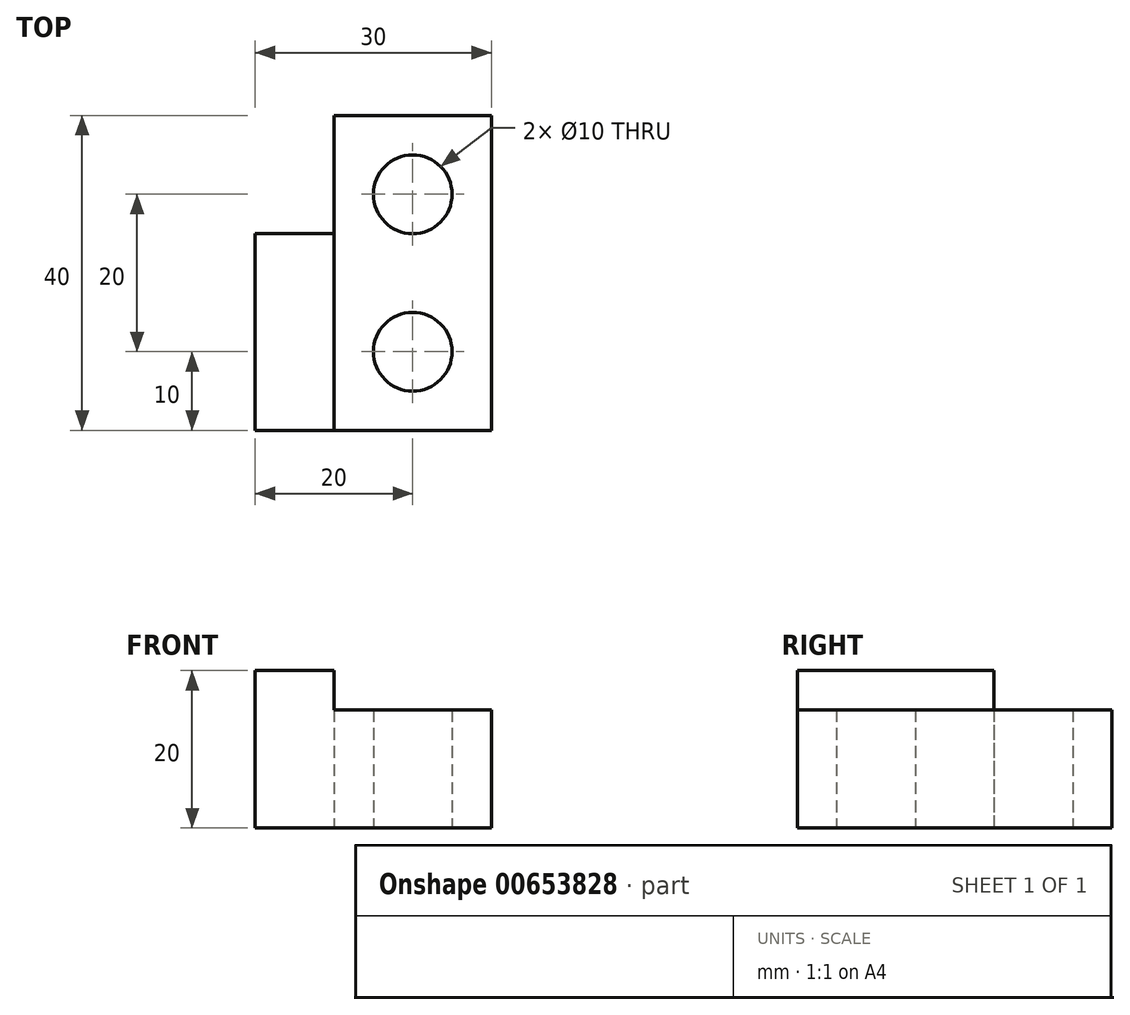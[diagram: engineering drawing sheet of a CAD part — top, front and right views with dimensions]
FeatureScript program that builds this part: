
annotation { "Feature Type Name" : "Feature", "Feature Type Description" : "" }
export const myFeature = defineFeature(function(context is Context, id is Id, definition is map)
    precondition{}
    {
        {
            var Q0;
            Q0=qCreatedBy(makeId("Top.planeOp"),FACE);
            var sketch = newSketch(context, id + "F0", { "sketchPlane" : qUnion([Q0])});
            skLineSegment(sketch, "E0.bottom", {"start": v(-10, -20) * mm, "end": v(10, -20) * mm});
            skLineSegment(sketch, "E0.top", {"start": v(-10, 20) * mm, "end": v(10, 20) * mm});
            skLineSegment(sketch, "E0.left", {"start": v(-10, -20) * mm, "end": v(-10, 20) * mm});
            skLineSegment(sketch, "E0.right", {"start": v(10, -20) * mm, "end": v(10, 20) * mm});
            skPoint(sketch, "E0.middle", {"position": v(0, 0) * mm});
            skLineSegment(sketch, "E1.bottom", {"start": v(-10, -20) * mm, "end": v(-20, -20) * mm});
            skLineSegment(sketch, "E1.top", {"start": v(-10, 5) * mm, "end": v(-20, 5) * mm});
            skLineSegment(sketch, "E1.left", {"start": v(-10, -20) * mm, "end": v(-10, 5) * mm});
            skLineSegment(sketch, "E1.right", {"start": v(-20, -20) * mm, "end": v(-20, 5) * mm});
            skCircle(sketch, "E2", {"center": v(0, 10) * mm, "radius": 5 * mm});
            skCircle(sketch, "E3", {"center": v(0, -10) * mm, "radius": 5 * mm});
            skSolve(sketch);
        }
        {
            var Q0;
            Q0=makeQuery(id+"F0.imprint","IMPRINT",FACE,{"disambiguationData":[TD([[makeQuery(id+"F0.imprint","IMPRINT",EDGE,{"derivedFrom":sQuery(id+"F0.wireOp",EDGE,"E0.bottom")}),1.0]])]});
            extrude(context, id + "F1", {"entities" : qUnion([Q0]), "depth" : 15 * mm, "offsetDistance" : 25 * mm});
        }
        {
            var Q0;
            Q0=makeQuery(id+"F0.imprint","IMPRINT",FACE,{"disambiguationData":[TD([[makeQuery(id+"F0.imprint","IMPRINT",EDGE,{"derivedFrom":sQuery(id+"F0.wireOp",EDGE,"E1.bottom")}),-1.0]])]});
            extrude(context, id + "F2", {"entities" : qUnion([Q0]), "operationType" : NewBodyOperationType.ADD, "depth" : 20 * mm, "offsetDistance" : 25 * mm});
        }
    });
